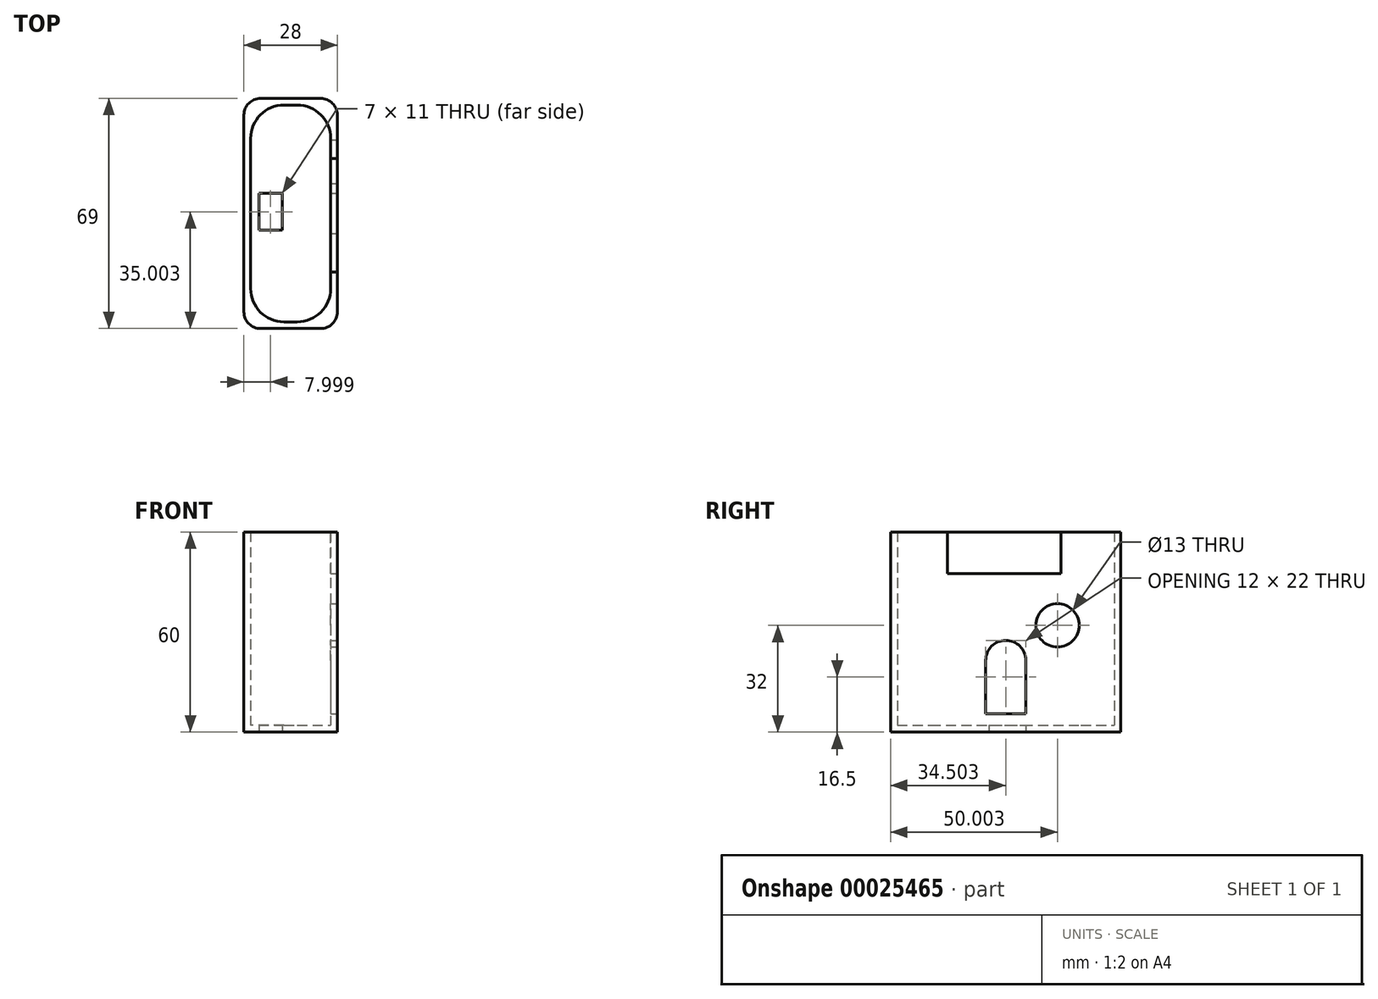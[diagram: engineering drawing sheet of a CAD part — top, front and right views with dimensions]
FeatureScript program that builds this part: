
annotation { "Feature Type Name" : "Feature", "Feature Type Description" : "" }
export const myFeature = defineFeature(function(context is Context, id is Id, definition is map)
    precondition{}
    {
        {
            var Q0;
            Q0=qCreatedBy(makeId("Top.planeOp"),FACE);
            var sketch = newSketch(context, id + "F0", { "sketchPlane" : qUnion([Q0])});
            skLineSegment(sketch, "E0.bottom", {"start": v(-17.5, -45.25) * mm, "end": v(10.5, -45.25) * mm});
            skLineSegment(sketch, "E0.top", {"start": v(-17.5, 23.75) * mm, "end": v(10.5, 23.75) * mm});
            skLineSegment(sketch, "E0.left", {"start": v(-17.5, -45.25) * mm, "end": v(-17.5, 23.75) * mm});
            skLineSegment(sketch, "E0.right", {"start": v(10.5, -45.25) * mm, "end": v(10.5, 23.75) * mm});
            skSolve(sketch);
        }
        {
            var Q0;
            Q0=makeQuery(id+"F0.imprint","IMPRINT",FACE,{"disambiguationData":[TD([[makeQuery(id+"F0.imprint","IMPRINT",EDGE,{"derivedFrom":sQuery(id+"F0.wireOp",EDGE,"E0.bottom")}),1.0]])]});
            extrude(context, id + "F1", {"entities" : qUnion([Q0]), "depth" : 60 * mm});
        }
        {
            var Q0;
            Q0=makeQuery(id+"F1.opExtrude","CAP_FACE",FACE,{"disambiguationData":[OSD([sQuery(id+"F0.wireOp",EDGE,"E0.bottom"),sQuery(id+"F0.wireOp",EDGE,"E0.top"),sQuery(id+"F0.wireOp",EDGE,"E0.left"),sQuery(id+"F0.wireOp",EDGE,"E0.right")])],"isStart":false});
            shell(context, id + "F2", {"entities" : qUnion([Q0]), "thickness" : 2 * mm});
        }
        {
            var Q0;
            Q0=makeQuery(id+"F1.opExtrude","SWEPT_FACE",FACE,{"disambiguationData":[OSD([sQuery(id+"F0.wireOp",EDGE,"E0.right")])]});
            var sketch = newSketch(context, id + "F3", { "sketchPlane" : qUnion([Q0])});
            skCircle(sketch, "E1", {"center": v(4.75, 32) * mm, "radius": 6.5 * mm});
            skPoint(sketch, "E2", {"position": v(-16.75, 5.5) * mm});
            skPoint(sketch, "E3", {"position": v(-4.75, 5.5) * mm});
            skLineSegment(sketch, "E4", {"start": v(-16.75, 5.5) * mm, "end": v(-4.75, 5.5) * mm});
            skLineSegment(sketch, "E5", {"start": v(-16.75, 5.5) * mm, "end": v(-16.75, 21.5) * mm});
            skLineSegment(sketch, "E6", {"start": v(-4.75, 5.5) * mm, "end": v(-4.75, 21.5) * mm});
            skArc(sketch, "E7", {"start": v(-4.75, 21.5) * mm, "mid": v(-10.75, 27.5) * mm, "end": v(-16.75, 21.5) * mm});
            skLineSegment(sketch, "E8", {"start": v(-10.75, 27.5) * mm, "end": v(-10.75, 47.5) * mm, "construction": true});
            skLineSegment(sketch, "E9.bottom", {"start": v(-10.75, 47.5) * mm, "end": v(5.75, 47.5) * mm});
            skLineSegment(sketch, "E9.top", {"start": v(-11.25, 88.5) * mm, "end": v(5.75, 88.5) * mm});
            skLineSegment(sketch, "E9.right", {"start": v(5.75, 47.5) * mm, "end": v(5.75, 88.5) * mm});
            skLineSegment(sketch, "E10.bottom", {"start": v(-11.25, 88.5) * mm, "end": v(-28.25, 88.5) * mm});
            skLineSegment(sketch, "E10.top", {"start": v(-11.25, 47.5) * mm, "end": v(-28.25, 47.5) * mm});
            skLineSegment(sketch, "E10.right", {"start": v(-28.25, 88.5) * mm, "end": v(-28.25, 47.5) * mm});
            skLineSegment(sketch, "E11", {"start": v(-11.25, 47.5) * mm, "end": v(-10.75, 47.5) * mm});
            skSolve(sketch);
        }
        {
            var Q0;
            Q0 = qSketchRegion(id + "F3", true);
            extrude(context, id + "F4", {"entities" : qUnion([Q0]), "operationType" : NewBodyOperationType.REMOVE, "oppositeDirection" : true, "depth" : 25 * mm});
        }
        {
            var Q0;
            Q0=makeQuery(id+"F2.opShell","OFFSET_EDGE",EDGE,{"disambiguationData":[OSD([sQuery(id+"F0.wireOp",EDGE,"E0.top"),sQuery(id+"F0.wireOp",EDGE,"E0.left")])]});
            fillet(context, id + "F5", {"entities" : qUnion([Q0]), "radius" : 10 * mm, "tangentPropagation" : true, "allowEdgeOverflow" : false});
        }
        {
            var Q0;
            Q0=makeQuery(id+"F2.opShell","OFFSET_EDGE",EDGE,{"disambiguationData":[OSD([sQuery(id+"F0.wireOp",EDGE,"E0.top"),sQuery(id+"F0.wireOp",EDGE,"E0.right")])]});
            fillet(context, id + "F6", {"entities" : qUnion([Q0]), "radius" : 10 * mm, "tangentPropagation" : true, "allowEdgeOverflow" : false});
        }
        {
            var Q0;
            Q0=makeQuery(id+"F2.opShell","OFFSET_EDGE",EDGE,{"disambiguationData":[OSD([sQuery(id+"F0.wireOp",EDGE,"E0.bottom"),sQuery(id+"F0.wireOp",EDGE,"E0.left")])]});
            fillet(context, id + "F7", {"entities" : qUnion([Q0]), "radius" : 10 * mm, "tangentPropagation" : true, "allowEdgeOverflow" : false});
        }
        {
            var Q0;
            Q0=makeQuery(id+"F2.opShell","OFFSET_EDGE",EDGE,{"disambiguationData":[OSD([sQuery(id+"F0.wireOp",EDGE,"E0.bottom"),sQuery(id+"F0.wireOp",EDGE,"E0.right")])]});
            fillet(context, id + "F8", {"entities" : qUnion([Q0]), "radius" : 10 * mm, "tangentPropagation" : true, "allowEdgeOverflow" : false});
        }
        {
            var Q0;
            Q0=makeQuery(id+"F1.opExtrude","SWEPT_EDGE",EDGE,{"disambiguationData":[OSD([sQuery(id+"F0.wireOp",EDGE,"E0.bottom"),sQuery(id+"F0.wireOp",EDGE,"E0.left")])]});
            fillet(context, id + "F9", {"entities" : qUnion([Q0]), "radius" : 5 * mm, "tangentPropagation" : true, "allowEdgeOverflow" : false});
        }
        {
            var Q0;
            Q0=makeQuery(id+"F1.opExtrude","SWEPT_EDGE",EDGE,{"disambiguationData":[OSD([sQuery(id+"F0.wireOp",EDGE,"E0.bottom"),sQuery(id+"F0.wireOp",EDGE,"E0.right")])]});
            fillet(context, id + "F10", {"entities" : qUnion([Q0]), "radius" : 5 * mm, "tangentPropagation" : true, "allowEdgeOverflow" : false});
        }
        {
            var Q0;
            Q0=makeQuery(id+"F1.opExtrude","SWEPT_EDGE",EDGE,{"disambiguationData":[OSD([sQuery(id+"F0.wireOp",EDGE,"E0.top"),sQuery(id+"F0.wireOp",EDGE,"E0.right")])]});
            fillet(context, id + "F11", {"entities" : qUnion([Q0]), "radius" : 5 * mm, "tangentPropagation" : true, "allowEdgeOverflow" : false});
        }
        {
            var Q0;
            Q0=makeQuery(id+"F1.opExtrude","SWEPT_EDGE",EDGE,{"disambiguationData":[OSD([sQuery(id+"F0.wireOp",EDGE,"E0.top"),sQuery(id+"F0.wireOp",EDGE,"E0.left")])]});
            fillet(context, id + "F12", {"entities" : qUnion([Q0]), "radius" : 5 * mm, "tangentPropagation" : true, "allowEdgeOverflow" : false});
        }
        {
            var Q0;
            Q0=qCreatedBy(makeId("Top.planeOp"),FACE);
            var sketch = newSketch(context, id + "F13", { "sketchPlane" : qUnion([Q0])});
            skLineSegment(sketch, "E12.bottom", {"start": v(-13, -15.75) * mm, "end": v(-6, -15.75) * mm});
            skLineSegment(sketch, "E12.top", {"start": v(-13, -4.75) * mm, "end": v(-6, -4.75) * mm});
            skLineSegment(sketch, "E12.right", {"start": v(-6, -15.75) * mm, "end": v(-6, -4.75) * mm});
            skLineSegment(sketch, "E12.left", {"start": v(-13, -15.75) * mm, "end": v(-13, -4.75) * mm});
            skSolve(sketch);
        }
        {
            var Q0;
            Q0 = qSketchRegion(id + "F13", true);
            var Q1;
            Q1=makeQuery(id+"F1.opExtrude","SWEPT_BODY",BODY,{"disambiguationData":[OSD([sQuery(id+"F0.wireOp",EDGE,"E0.bottom"),sQuery(id+"F0.wireOp",EDGE,"E0.top"),sQuery(id+"F0.wireOp",EDGE,"E0.left"),sQuery(id+"F0.wireOp",EDGE,"E0.right")])]});
            extrude(context, id + "F14", {"entities" : qUnion([Q0]), "operationType" : NewBodyOperationType.REMOVE, "endBound" : BoundingType.UP_TO_BODY, "endBoundEntityBody" : qUnion([Q1]), "depth" : 4 * mm});
        }
    });
